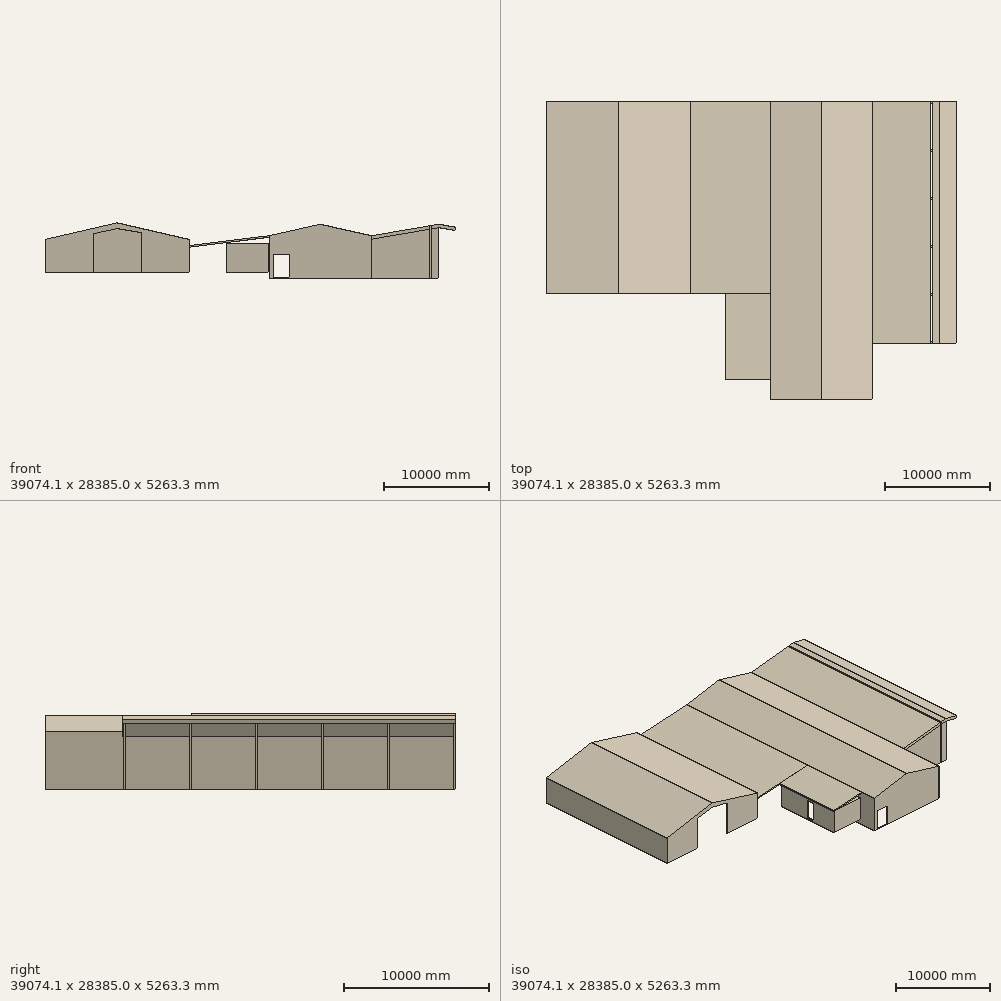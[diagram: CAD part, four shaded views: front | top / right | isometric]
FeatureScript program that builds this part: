
annotation { "Feature Type Name" : "Feature", "Feature Type Description" : "" }
export const myFeature = defineFeature(function(context is Context, id is Id, definition is map)
    precondition{}
    {
        {
            var Q0;
            Q0=qCreatedBy(makeId("Front.planeOp"),FACE);
            var sketch = newSketch(context, id + "F0", { "sketchPlane" : qUnion([Q0]), "disableImprinting" : false});
            skLineSegment(sketch, "E0.bottom", {"start": v(-4547.6, 1514.38) * mm, "end": v(5212.4, 1514.38) * mm});
            skLineSegment(sketch, "E0.top", {"start": v(-4547.6, -2515.62) * mm, "end": v(5212.4, -2515.62) * mm});
            skLineSegment(sketch, "E0.left", {"start": v(-4547.6, 1514.38) * mm, "end": v(-4547.6, -2515.62) * mm});
            skLineSegment(sketch, "E0.right", {"start": v(5212.4, 1514.38) * mm, "end": v(5212.4, -2515.62) * mm});
            skPoint(sketch, "E1", {"position": v(-3132, 1514.38) * mm});
            skPoint(sketch, "E2", {"position": v(-379.4, 3011.24) * mm});
            skLineSegment(sketch, "E3", {"start": v(-4547.6, 1514.38) * mm, "end": v(332.4, 2614.38) * mm});
            skLineSegment(sketch, "E4", {"start": v(5212.4, 1514.38) * mm, "end": v(332.4, 2614.38) * mm});
            skLineSegment(sketch, "E5.bottom", {"start": v(-12157.6, -1935.62) * mm, "end": v(-25873.6, -1935.62) * mm});
            skLineSegment(sketch, "E5.top", {"start": v(-12157.6, 1164.38) * mm, "end": v(-25873.6, 1164.38) * mm});
            skLineSegment(sketch, "E5.left", {"start": v(-12157.6, -1935.62) * mm, "end": v(-12157.6, 1164.38) * mm});
            skLineSegment(sketch, "E5.right", {"start": v(-25873.6, -1935.62) * mm, "end": v(-25873.6, 1164.38) * mm});
            skLineSegment(sketch, "E6", {"start": v(-25873.6, 1164.38) * mm, "end": v(-19015.6, 2747.68) * mm});
            skPoint(sketch, "E6.endSnap0", {"position": v(-19015.6, 1164.38) * mm});
            skLineSegment(sketch, "E7", {"start": v(-19015.6, 2747.68) * mm, "end": v(-12157.6, 1164.38) * mm});
            skLineSegment(sketch, "E8", {"start": v(-12157.6, 580) * mm, "end": v(-4547.6, 1514.38) * mm});
            skLineSegment(sketch, "E9", {"start": v(-12157.6, 580) * mm, "end": v(-12157.6, 428.86) * mm});
            skLineSegment(sketch, "E10", {"start": v(-12157.6, 428.86) * mm, "end": v(-4547.6, 1363.25) * mm});
            skLineSegment(sketch, "E11", {"start": v(-4547.6, 1363.25) * mm, "end": v(-4547.6, 1514.38) * mm});
            skLineSegment(sketch, "E12", {"start": v(5212.4, 1514.38) * mm, "end": v(11618.64, 2614.38) * mm});
            skLineSegment(sketch, "E13", {"start": v(11618.64, 2614.38) * mm, "end": v(13200.49, 2342.77) * mm});
            skLineSegment(sketch, "E14", {"start": v(10917.4, -2515.62) * mm, "end": v(10917.4, 2493.97) * mm});
            skLineSegment(sketch, "E15", {"start": v(10767.4, -2515.62) * mm, "end": v(10767.4, 2468.22) * mm});
            skLineSegment(sketch, "E16", {"start": v(10767.4, -2515.62) * mm, "end": v(10917.4, -2515.62) * mm});
            skLineSegment(sketch, "E17.0", {"start": v(5267.4, 1194.07) * mm, "end": v(11618.64, 2284.63) * mm});
            skLineSegment(sketch, "E18", {"start": v(5267.4, 1194.07) * mm, "end": v(5212.4, 1184.63) * mm});
            skLineSegment(sketch, "E19.0", {"start": v(11618.64, 2284.63) * mm, "end": v(13145.5, 2022.46) * mm});
            skLineSegment(sketch, "E20", {"start": v(13145.5, 2022.46) * mm, "end": v(13200.49, 2342.77) * mm});
            skLineSegment(sketch, "E21", {"start": v(5212.4, -2515.62) * mm, "end": v(11618.64, -2515.62) * mm});
            skLineSegment(sketch, "E22", {"start": v(11618.64, -2515.62) * mm, "end": v(11618.64, 2284.63) * mm});
            skSolve(sketch);
        }
        {
            var Q0;
            Q0=makeQuery(id+"F0.imprint","IMPRINT",FACE,{"disambiguationData":[TD([[makeQuery(id+"F0.imprint","IMPRINT",EDGE,{"derivedFrom":sQuery(id+"F0.wireOp",EDGE,"E0.bottom")}),-1.0]])]});
            var Q1;
            Q1=makeQuery(id+"F0.imprint","IMPRINT",FACE,{"disambiguationData":[TD([[makeQuery(id+"F0.imprint","IMPRINT",EDGE,{"derivedFrom":sQuery(id+"F0.wireOp",EDGE,"E0.bottom")}),1.0]])]});
            extrude(context, id + "F1", {"entities" : qUnion([Q0, Q1]), "depth" : 28385 * mm});
        }
        {
            var Q0;
            {var subQ3=sQuery(id+"F0.wireOp",EDGE,"E5.bottom");Q0=makeQuery(id+"F0.imprint","IMPRINT",FACE,{"disambiguationData":[TD([[makeQuery(id+"F0.imprint","IMPRINT",EDGE,{"derivedFrom":subQ3}),-1.0]])]});}
            var Q1;
            Q1=makeQuery(id+"F0.imprint","IMPRINT",FACE,{"disambiguationData":[TD([[makeQuery(id+"F0.imprint","IMPRINT",EDGE,{"derivedFrom":sQuery(id+"F0.wireOp",EDGE,"E5.top")}),-1.0]])]});
            extrude(context, id + "F2", {"entities" : qUnion([Q0, Q1]), "depth" : 18288 * mm});
        }
        {
            var Q0;
            Q0=makeQuery(id+"F0.imprint","IMPRINT",FACE,{"disambiguationData":[TD([[makeQuery(id+"F0.imprint","IMPRINT",EDGE,{"derivedFrom":sQuery(id+"F0.wireOp",EDGE,"E8")}),-1.0]])]});
            var Q1;
            Q1=makeQuery(id+"F2.opExtrude","CAP_FACE",FACE,{"disambiguationData":[OSD([sQuery(id+"F0.wireOp",EDGE,"E5.bottom"),sQuery(id+"F0.wireOp",EDGE,"E5.left"),sQuery(id+"F0.wireOp",EDGE,"E5.right"),sQuery(id+"F0.wireOp",EDGE,"E6"),sQuery(id+"F0.wireOp",EDGE,"E7"),sQuery(id+"F0.wireOp",EDGE,"E9")])],"isStart":false});
            extrude(context, id + "F3", {"entities" : qUnion([Q0]), "endBound" : BoundingType.UP_TO_SURFACE, "endBoundEntityFace" : qUnion([Q1]), "depth" : 25 * mm});
        }
        {
            var Q0;
            Q0=sQuery(id+"F0.wireOp",EDGE,"E12");
            var Q1;
            Q1=sQuery(id+"F0.wireOp",EDGE,"E13");
            extrude(context, id + "F4", {"bodyType" : ExtendedToolBodyType.SURFACE, "surfaceEntities" : qUnion([Q0, Q1]), "depth" : 23050 * mm});
        }
        {
            var Q0;
            {var subQ0=sQuery(id+"F0.wireOp",EDGE,"E14");Q0=makeQuery(id+"F0.imprint","IMPRINT",FACE,{"disambiguationData":[TD([[makeQuery(id+"F0.imprint","IMPRINT",EDGE,{"derivedFrom":subQ0}),1.0]])]});}
            extrude(context, id + "F5", {"entities" : qUnion([Q0]), "depth" : 150 * mm});
        }
        {
            var Q0;
            Q0=makeQuery(id+"F2.opExtrude","SWEPT_FACE",FACE,{"disambiguationData":[OSD([sQuery(id+"F0.wireOp",EDGE,"E5.bottom")])]});
            var Q1;
            Q1=makeQuery(id+"F1.opExtrude","SWEPT_FACE",FACE,{"disambiguationData":[OSD([sQuery(id+"F0.wireOp",EDGE,"E0.top")])]});
            shell(context, id + "F6", {"entities" : qUnion([Q0, Q1]), "thickness" : 150 * mm});
        }
        {
            var Q0;
            Q0=makeQuery(id+"F5.opExtrude","SWEPT_BODY",BODY,{"disambiguationData":[OSD([sQuery(id+"F0.wireOp",EDGE,"E12"),sQuery(id+"F0.wireOp",EDGE,"E14"),sQuery(id+"F0.wireOp",EDGE,"E15"),sQuery(id+"F0.wireOp",EDGE,"E16")])]});
            transform(context, id + "F7", {"entities" : qUnion([Q0]), "transformType" : TransformType.TRANSLATION_3D, "dx" : 4572 * mm, "dy" : 0 * mm, "dz" : 0 * mm, "makeCopy" : true});
        }
        {
            var Q0;
            Q0=makeQuery(id+"F7.opPattern","COPY",BODY,{"derivedFrom":makeQuery(id+"F5.opExtrude","SWEPT_BODY",BODY,{"disambiguationData":[OSD([sQuery(id+"F0.wireOp",EDGE,"E12"),sQuery(id+"F0.wireOp",EDGE,"E14"),sQuery(id+"F0.wireOp",EDGE,"E15"),sQuery(id+"F0.wireOp",EDGE,"E16")])]}),"instanceName":"1"});
            deleteBodies(context, id + "F8", {"entities" : qUnion([Q0])});
        }
        {
            var Q0;
            Q0=makeQuery(id+"F5.opExtrude","SWEPT_BODY",BODY,{"disambiguationData":[OSD([sQuery(id+"F0.wireOp",EDGE,"E12"),sQuery(id+"F0.wireOp",EDGE,"E14"),sQuery(id+"F0.wireOp",EDGE,"E15"),sQuery(id+"F0.wireOp",EDGE,"E16")])]});
            transform(context, id + "F9", {"entities" : qUnion([Q0]), "transformType" : TransformType.TRANSLATION_3D, "dx" : 0 * mm, "dy" : -4572 * mm, "dz" : 0 * mm, "makeCopy" : true});
        }
        {
            var Q0;
            Q0=makeQuery(id+"F9.opPattern","COPY",BODY,{"derivedFrom":makeQuery(id+"F5.opExtrude","SWEPT_BODY",BODY,{"disambiguationData":[OSD([sQuery(id+"F0.wireOp",EDGE,"E12"),sQuery(id+"F0.wireOp",EDGE,"E14"),sQuery(id+"F0.wireOp",EDGE,"E15"),sQuery(id+"F0.wireOp",EDGE,"E16")])]}),"instanceName":"1"});
            transform(context, id + "F10", {"entities" : qUnion([Q0]), "transformType" : TransformType.TRANSLATION_3D, "dx" : 0 * mm, "dy" : -4572 * mm, "dz" : 0 * mm, "makeCopy" : true});
        }
        {
            var Q0;
            Q0=makeQuery(id+"F5.opExtrude","SWEPT_BODY",BODY,{"disambiguationData":[OSD([sQuery(id+"F0.wireOp",EDGE,"E12"),sQuery(id+"F0.wireOp",EDGE,"E14"),sQuery(id+"F0.wireOp",EDGE,"E15"),sQuery(id+"F0.wireOp",EDGE,"E16")])]});
            transform(context, id + "F11", {"entities" : qUnion([Q0]), "transformType" : TransformType.TRANSLATION_3D, "dx" : 0 * mm, "dy" : ((-4572) * 3) * mm, "dz" : 0 * mm, "makeCopy" : true});
        }
        {
            var Q0;
            Q0=makeQuery(id+"F5.opExtrude","SWEPT_BODY",BODY,{"disambiguationData":[OSD([sQuery(id+"F0.wireOp",EDGE,"E12"),sQuery(id+"F0.wireOp",EDGE,"E14"),sQuery(id+"F0.wireOp",EDGE,"E15"),sQuery(id+"F0.wireOp",EDGE,"E16")])]});
            transform(context, id + "F12", {"entities" : qUnion([Q0]), "transformType" : TransformType.TRANSLATION_3D, "dx" : 0 * mm, "dy" : (-4572 * 4) * mm, "dz" : 0 * mm, "makeCopy" : true});
        }
        {
            var Q0;
            Q0=makeQuery(id+"F5.opExtrude","SWEPT_BODY",BODY,{"disambiguationData":[OSD([sQuery(id+"F0.wireOp",EDGE,"E12"),sQuery(id+"F0.wireOp",EDGE,"E14"),sQuery(id+"F0.wireOp",EDGE,"E15"),sQuery(id+"F0.wireOp",EDGE,"E16")])]});
            transform(context, id + "F13", {"entities" : qUnion([Q0]), "transformType" : TransformType.TRANSLATION_3D, "dx" : 0 * mm, "dy" : (-4572 * 5) * mm, "dz" : 0 * mm, "makeCopy" : true});
        }
        {
            var Q0;
            {var subQ6=sQuery(id+"F0.wireOp",EDGE,"E13");Q0=makeQuery(id+"F0.imprint","IMPRINT",FACE,{"disambiguationData":[TD([[makeQuery(id+"F0.imprint","IMPRINT",EDGE,{"derivedFrom":subQ6}),-1.0]])]});}
            var Q1;
            {var subQ0=sQuery(id+"F0.wireOp",EDGE,"E18");Q1=makeQuery(id+"F0.imprint","IMPRINT",FACE,{"disambiguationData":[TD([[makeQuery(id+"F0.imprint","IMPRINT",EDGE,{"derivedFrom":subQ0}),-1.0]])]});}
            extrude(context, id + "F14", {"entities" : qUnion([Q0, Q1]), "depth" : 23050 * mm});
        }
        {
            var Q0;
            Q0=makeQuery(id+"F1.opExtrude","CAP_FACE",FACE,{"disambiguationData":[OSD([sQuery(id+"F0.wireOp",EDGE,"E0.top"),sQuery(id+"F0.wireOp",EDGE,"E0.left"),sQuery(id+"F0.wireOp",EDGE,"E0.right"),sQuery(id+"F0.wireOp",EDGE,"E3"),sQuery(id+"F0.wireOp",EDGE,"E4"),sQuery(id+"F0.wireOp",EDGE,"E11")])],"isStart":false});
            var sketch = newSketch(context, id + "F15", { "sketchPlane" : qUnion([Q0])});
            skSolve(sketch);
        }
        {
            var Q0;
            {var subQ5=sQuery(id+"F0.wireOp",EDGE,"E22");Q0=makeQuery(id+"F0.imprint","IMPRINT",FACE,{"disambiguationData":[TD([[makeQuery(id+"F0.imprint","IMPRINT",EDGE,{"derivedFrom":subQ5}),1.0]])]});}
            var Q1;
            {var subQ0=sQuery(id+"F0.wireOp",EDGE,"E18");Q1=makeQuery(id+"F0.imprint","IMPRINT",FACE,{"disambiguationData":[TD([[makeQuery(id+"F0.imprint","IMPRINT",EDGE,{"derivedFrom":subQ0}),1.0]])]});}
            extrude(context, id + "F16", {"entities" : qUnion([Q0, Q1]), "depth" : 25 * mm});
        }
        {
            var Q0;
            Q0=makeQuery(id+"F16.opExtrude","SWEPT_BODY",BODY,{"disambiguationData":[OSD([sQuery(id+"F0.wireOp",EDGE,"E14"),sQuery(id+"F0.wireOp",EDGE,"E17.0"),sQuery(id+"F0.wireOp",EDGE,"E21"),sQuery(id+"F0.wireOp",EDGE,"E22")])]});
            var Q1;
            Q1=makeQuery(id+"F16.opExtrude","SWEPT_BODY",BODY,{"disambiguationData":[OSD([sQuery(id+"F0.wireOp",EDGE,"E0.right"),sQuery(id+"F0.wireOp",EDGE,"E15"),sQuery(id+"F0.wireOp",EDGE,"E17.0"),sQuery(id+"F0.wireOp",EDGE,"E18"),sQuery(id+"F0.wireOp",EDGE,"E21")])]});
            transform(context, id + "F17", {"entities" : qUnion([Q0, Q1]), "transformType" : TransformType.TRANSLATION_3D, "dx" : 0 * mm, "dy" : -23025 * mm, "dz" : 0 * mm, "makeCopy" : true});
        }
        {
            var Q0;
            Q0=makeQuery(id+"F15.imprint","IMPRINT",FACE,{"disambiguationData":[TD([[makeQuery(id+"F15.imprint","IMPRINT",EDGE,{"derivedFrom":makeQuery(id+"F1.opExtrude","CAP_EDGE",EDGE,{"disambiguationData":[OSD([sQuery(id+"F0.wireOp",EDGE,"E0.top")])],"isStart":false})}),1.0]])]});
            var sketch = newSketch(context, id + "F18", { "sketchPlane" : qUnion([Q0])});
            skLineSegment(sketch, "E23.bottom", {"start": v(-4109.24, -2494.23) * mm, "end": v(-2637.3, -2494.23) * mm});
            skLineSegment(sketch, "E23.top", {"start": v(-4109.24, -221.76) * mm, "end": v(-2637.3, -221.76) * mm});
            skLineSegment(sketch, "E23.left", {"start": v(-4109.24, -2494.23) * mm, "end": v(-4109.24, -221.76) * mm});
            skLineSegment(sketch, "E23.right", {"start": v(-2637.3, -2494.23) * mm, "end": v(-2637.3, -221.76) * mm});
            skSolve(sketch);
        }
        {
            var Q0;
            Q0 = qSketchRegion(id + "F18", true);
            extrude(context, id + "F19", {"entities" : qUnion([Q0]), "operationType" : NewBodyOperationType.REMOVE, "oppositeDirection" : true, "depth" : 200 * mm});
        }
        {
            var Q0;
            {var subQ1=sQuery(id+"F0.wireOp",EDGE,"E0.bottom");Q0=makeQuery(id+"F0.imprint","IMPRINT",FACE,{"disambiguationData":[TD([[makeQuery(id+"F0.imprint","IMPRINT",EDGE,{"derivedFrom":subQ1}),-1.0]])]});}
            var sketch = newSketch(context, id + "F20", { "sketchPlane" : qUnion([Q0])});
            skLineSegment(sketch, "E24.bottom", {"start": v(-4243.15, -2515.63) * mm, "end": v(207.97, -2515.63) * mm});
            skLineSegment(sketch, "E24.top", {"start": v(-4243.15, 1577.35) * mm, "end": v(207.97, 1577.35) * mm});
            skLineSegment(sketch, "E24.left", {"start": v(-4243.15, -2515.63) * mm, "end": v(-4243.15, 1577.35) * mm});
            skLineSegment(sketch, "E24.right", {"start": v(207.97, -2515.63) * mm, "end": v(207.97, 1577.35) * mm});
            skSolve(sketch);
        }
        {
            var Q0;
            Q0 = qSketchRegion(id + "F20", true);
            extrude(context, id + "F21", {"entities" : qUnion([Q0]), "operationType" : NewBodyOperationType.REMOVE, "depth" : 200 * mm});
        }
        {
            var Q0;
            Q0=makeQuery(id+"F2.opExtrude","CAP_FACE",FACE,{"disambiguationData":[OSD([sQuery(id+"F0.wireOp",EDGE,"E5.bottom"),sQuery(id+"F0.wireOp",EDGE,"E5.left"),sQuery(id+"F0.wireOp",EDGE,"E5.right"),sQuery(id+"F0.wireOp",EDGE,"E6"),sQuery(id+"F0.wireOp",EDGE,"E7"),sQuery(id+"F0.wireOp",EDGE,"E9")])],"isStart":false});
            var sketch = newSketch(context, id + "F22", { "sketchPlane" : qUnion([Q0])});
            skLineSegment(sketch, "E25", {"start": v(-21255.7, -1935.62) * mm, "end": v(-21255.7, 1715.16) * mm});
            skLineSegment(sketch, "E26", {"start": v(-21255.7, 1715.16) * mm, "end": v(-19015.6, 2198.75) * mm});
            skLineSegment(sketch, "E27", {"start": v(-19015.6, 2198.75) * mm, "end": v(-16755.7, 1818.38) * mm});
            skLineSegment(sketch, "E28", {"start": v(-16755.7, 1818.38) * mm, "end": v(-16755.7, -1935.62) * mm});
            skLineSegment(sketch, "E29", {"start": v(-16755.7, -1935.62) * mm, "end": v(-21255.7, -1935.62) * mm});
            skSolve(sketch);
        }
        {
            var Q0;
            Q0=makeQuery(id+"F22.imprint","IMPRINT",FACE,{"disambiguationData":[TD([[makeQuery(id+"F22.imprint","IMPRINT",EDGE,{"derivedFrom":sQuery(id+"F22.wireOp",EDGE,"E25")}),-1.0]])]});
            extrude(context, id + "F23", {"entities" : qUnion([Q0]), "operationType" : NewBodyOperationType.REMOVE, "oppositeDirection" : true, "depth" : 200 * mm});
        }
        {
            var Q0;
            Q0=makeQuery(id+"F2.opExtrude","CAP_FACE",FACE,{"disambiguationData":[OSD([sQuery(id+"F0.wireOp",EDGE,"E5.bottom"),sQuery(id+"F0.wireOp",EDGE,"E5.left"),sQuery(id+"F0.wireOp",EDGE,"E5.right"),sQuery(id+"F0.wireOp",EDGE,"E6"),sQuery(id+"F0.wireOp",EDGE,"E7"),sQuery(id+"F0.wireOp",EDGE,"E9")])],"isStart":false});
            cPlane(context, id + "F24", {"entities" : qUnion([Q0]), "cplaneType" : CPlaneType.OFFSET, "offset" : 25 * mm, "width" : 150 * mm, "height" : 150 * mm});
        }
        {
            var Q0;
            Q0=qCreatedBy(id+"F24.planeOp",FACE);
            var sketch = newSketch(context, id + "F25", { "sketchPlane" : qUnion([Q0])});
            skLineSegment(sketch, "E30.bottom", {"start": v(-8594.12, -1935.62) * mm, "end": v(-4631.55, -1935.62) * mm});
            skLineSegment(sketch, "E30.top", {"start": v(-8594.12, 769.92) * mm, "end": v(-4631.55, 769.92) * mm});
            skLineSegment(sketch, "E30.left", {"start": v(-8594.12, -1935.62) * mm, "end": v(-8594.12, 769.92) * mm});
            skLineSegment(sketch, "E30.right", {"start": v(-4631.55, -1935.62) * mm, "end": v(-4631.55, 769.92) * mm});
            skLineSegment(sketch, "E31", {"start": v(-4552, 1524) * mm, "end": v(-8812.7, 997.2) * mm});
            skLineSegment(sketch, "E32", {"start": v(-8812.7, 997.2) * mm, "end": v(-8793.94, 845.43) * mm});
            skLineSegment(sketch, "E33", {"start": v(-8793.94, 845.43) * mm, "end": v(-4554.4, 1369.62) * mm});
            skLineSegment(sketch, "E34", {"start": v(-4554.4, 1369.62) * mm, "end": v(-4552, 1524) * mm});
            skSolve(sketch);
        }
        {
            var Q0;
            Q0=makeQuery(id+"F25.imprint","IMPRINT",FACE,{"disambiguationData":[TD([[makeQuery(id+"F25.imprint","IMPRINT",EDGE,{"derivedFrom":sQuery(id+"F25.wireOp",EDGE,"E30.bottom")}),1.0]])]});
            extrude(context, id + "F26", {"entities" : qUnion([Q0]), "depth" : 8000 * mm});
        }
        {
            var Q0;
            Q0=makeQuery(id+"F26.opExtrude","SWEPT_FACE",FACE,{"disambiguationData":[OSD([sQuery(id+"F25.wireOp",EDGE,"E30.left")])]});
            var sketch = newSketch(context, id + "F27", { "sketchPlane" : qUnion([Q0])});
            skPoint(sketch, "E35.firstSnap0", {"position": v(22313, -1935.62) * mm});
            skLineSegment(sketch, "E35.bottom", {"start": v(22313, -1718.62) * mm, "end": v(23251.25, -1718.62) * mm});
            skLineSegment(sketch, "E35.top", {"start": v(22313, 404.78) * mm, "end": v(23251.25, 404.78) * mm});
            skLineSegment(sketch, "E35.left", {"start": v(22313, -1718.62) * mm, "end": v(22313, 404.78) * mm});
            skLineSegment(sketch, "E35.right", {"start": v(23251.25, -1718.62) * mm, "end": v(23251.25, 404.78) * mm});
            skSolve(sketch);
        }
        {
            var Q0;
            Q0=makeQuery(id+"F26.opExtrude","SWEPT_FACE",FACE,{"disambiguationData":[OSD([sQuery(id+"F25.wireOp",EDGE,"E30.bottom")])]});
            shell(context, id + "F28", {"entities" : qUnion([Q0]), "thickness" : 100 * mm});
        }
        {
            var Q0;
            Q0=makeQuery(id+"F27.imprint","IMPRINT",FACE,{"disambiguationData":[TD([[makeQuery(id+"F27.imprint","IMPRINT",EDGE,{"derivedFrom":sQuery(id+"F27.wireOp",EDGE,"E35.bottom")}),1.0]])]});
            extrude(context, id + "F29", {"entities" : qUnion([Q0]), "operationType" : NewBodyOperationType.REMOVE, "oppositeDirection" : true, "depth" : 105 * mm});
        }
        {
            var Q0;
            Q0=makeQuery(id+"F25.imprint","IMPRINT",FACE,{"disambiguationData":[TD([[makeQuery(id+"F25.imprint","IMPRINT",EDGE,{"derivedFrom":sQuery(id+"F25.wireOp",EDGE,"E31")}),1.0]])]});
            extrude(context, id + "F30", {"entities" : qUnion([Q0]), "depth" : 8200 * mm});
        }
    });
